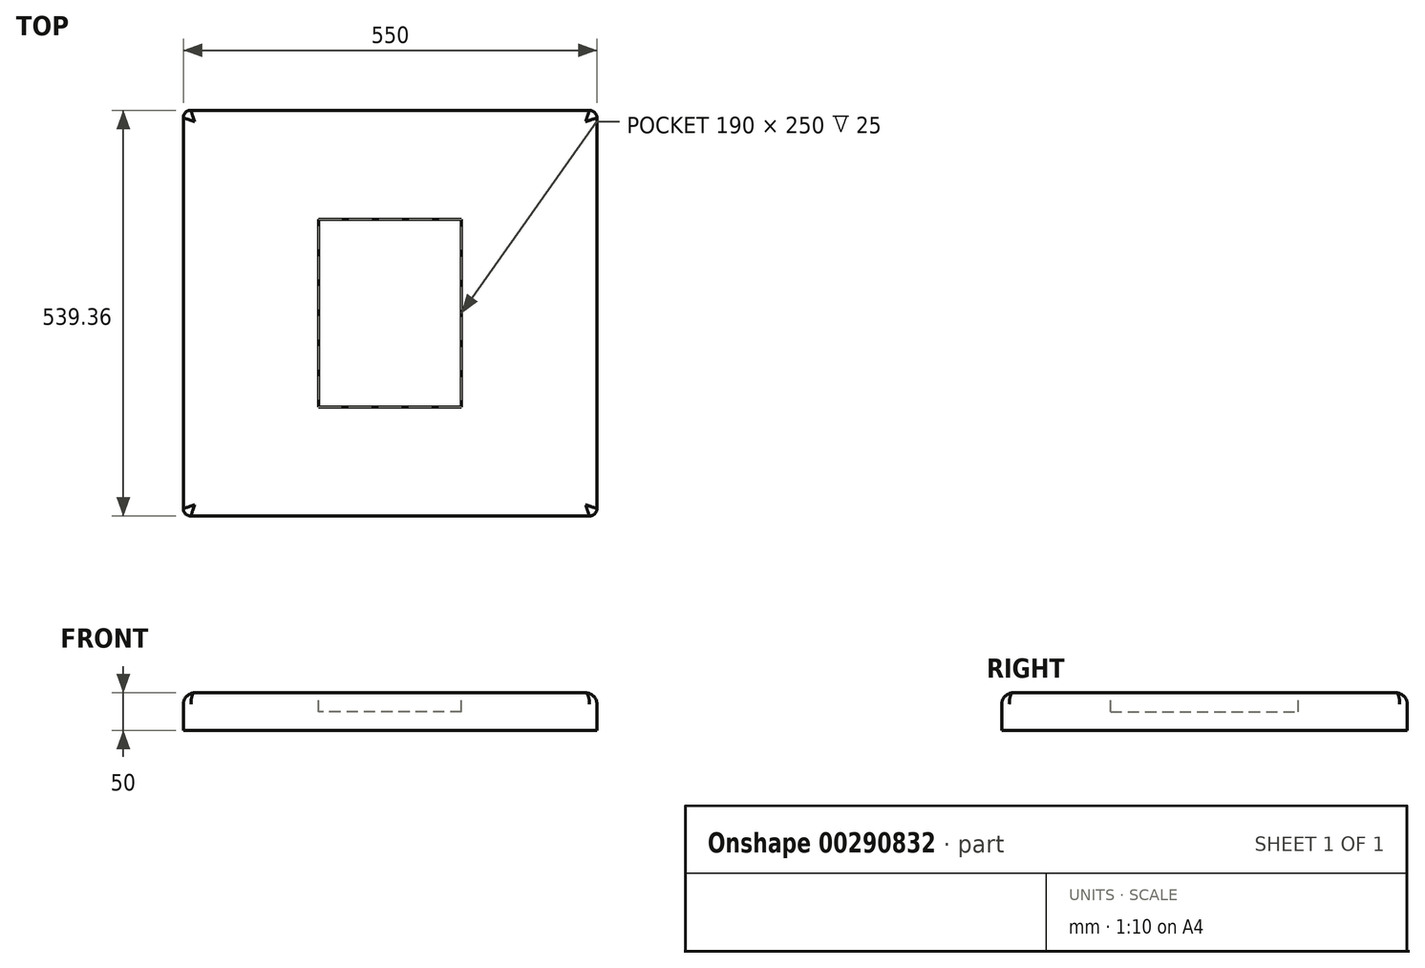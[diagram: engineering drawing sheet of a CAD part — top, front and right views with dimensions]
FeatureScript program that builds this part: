
annotation { "Feature Type Name" : "Feature", "Feature Type Description" : "" }
export const myFeature = defineFeature(function(context is Context, id is Id, definition is map)
    precondition{}
    {
        {
            var Q0;
            Q0=qCreatedBy(makeId("Top.planeOp"),FACE);
            var sketch = newSketch(context, id + "F0", { "sketchPlane" : qUnion([Q0])});
            skLineSegment(sketch, "E0.bottom", {"start": v(275, -269.68) * mm, "end": v(-275, -269.68) * mm});
            skLineSegment(sketch, "E0.top", {"start": v(275, 269.68) * mm, "end": v(-275, 269.68) * mm});
            skLineSegment(sketch, "E0.left", {"start": v(275, -269.68) * mm, "end": v(275, 269.68) * mm});
            skLineSegment(sketch, "E0.right", {"start": v(-275, -269.68) * mm, "end": v(-275, 269.68) * mm});
            skPoint(sketch, "E0.middle", {"position": v(0, 0) * mm});
            skSolve(sketch);
        }
        {
            var Q0;
            Q0=makeQuery(id+"F0.imprint","IMPRINT",FACE,{"disambiguationData":[TD([[makeQuery(id+"F0.imprint","IMPRINT",EDGE,{"derivedFrom":sQuery(id+"F0.wireOp",EDGE,"E0.bottom")}),-1.0]])]});
            extrude(context, id + "F1", {"entities" : qUnion([Q0]), "depth" : 50 * mm});
        }
        {
            var Q0;
            Q0=makeQuery(id+"F1.opExtrude","CAP_EDGE",EDGE,{"disambiguationData":[OSD([sQuery(id+"F0.wireOp",EDGE,"E0.bottom")])],"isStart":false});
            var Q1;
            Q1=makeQuery(id+"F1.opExtrude","CAP_EDGE",EDGE,{"disambiguationData":[OSD([sQuery(id+"F0.wireOp",EDGE,"E0.left")])],"isStart":false});
            var Q2;
            Q2=makeQuery(id+"F1.opExtrude","CAP_EDGE",EDGE,{"disambiguationData":[OSD([sQuery(id+"F0.wireOp",EDGE,"E0.top")])],"isStart":false});
            var Q3;
            Q3=makeQuery(id+"F1.opExtrude","CAP_EDGE",EDGE,{"disambiguationData":[OSD([sQuery(id+"F0.wireOp",EDGE,"E0.right")])],"isStart":false});
            fillet(context, id + "F2", {"entities" : qUnion([Q0, Q1, Q2, Q3]), "radius" : 15 * mm, "tangentPropagation" : true, "allowEdgeOverflow" : false});
        }
        {
            var Q0;
            Q0=makeQuery(id+"F1.opExtrude","CAP_FACE",FACE,{"disambiguationData":[OSD([sQuery(id+"F0.wireOp",EDGE,"E0.bottom"),sQuery(id+"F0.wireOp",EDGE,"E0.top"),sQuery(id+"F0.wireOp",EDGE,"E0.left"),sQuery(id+"F0.wireOp",EDGE,"E0.right")])],"isStart":false});
            var sketch = newSketch(context, id + "F3", { "sketchPlane" : qUnion([Q0])});
            skLineSegment(sketch, "E1.bottom", {"start": v(95, -125) * mm, "end": v(-95, -125) * mm});
            skLineSegment(sketch, "E1.top", {"start": v(95, 125) * mm, "end": v(-95, 125) * mm});
            skLineSegment(sketch, "E1.left", {"start": v(95, -125) * mm, "end": v(95, 125) * mm});
            skLineSegment(sketch, "E1.right", {"start": v(-95, -125) * mm, "end": v(-95, 125) * mm});
            skPoint(sketch, "E1.middle", {"position": v(0, 0) * mm});
            skSolve(sketch);
        }
        {
            var Q0;
            Q0=makeQuery(id+"F3.imprint","IMPRINT",FACE,{"disambiguationData":[TD([[makeQuery(id+"F3.imprint","IMPRINT",EDGE,{"derivedFrom":sQuery(id+"F3.wireOp",EDGE,"E1.bottom")}),-1.0]])]});
            extrude(context, id + "F4", {"entities" : qUnion([Q0]), "operationType" : NewBodyOperationType.REMOVE, "oppositeDirection" : true, "depth" : 25 * mm});
        }
        {
            var Q0;
            Q0=makeQuery(id+"F1.opExtrude","SWEPT_EDGE",EDGE,{"disambiguationData":[OSD([sQuery(id+"F0.wireOp",EDGE,"E0.bottom"),sQuery(id+"F0.wireOp",EDGE,"E0.left")])]});
            fillet(context, id + "F5", {"entities" : qUnion([Q0]), "radius" : 10 * mm, "tangentPropagation" : true, "allowEdgeOverflow" : false});
        }
        {
            var Q0;
            Q0=makeQuery(id+"F1.opExtrude","SWEPT_EDGE",EDGE,{"disambiguationData":[OSD([sQuery(id+"F0.wireOp",EDGE,"E0.bottom"),sQuery(id+"F0.wireOp",EDGE,"E0.right")])]});
            fillet(context, id + "F6", {"entities" : qUnion([Q0]), "radius" : 10 * mm, "tangentPropagation" : true, "allowEdgeOverflow" : false});
        }
        {
            var Q0;
            Q0=makeQuery(id+"F1.opExtrude","SWEPT_EDGE",EDGE,{"disambiguationData":[OSD([sQuery(id+"F0.wireOp",EDGE,"E0.top"),sQuery(id+"F0.wireOp",EDGE,"E0.left")])]});
            fillet(context, id + "F7", {"entities" : qUnion([Q0]), "radius" : 10 * mm, "tangentPropagation" : true, "allowEdgeOverflow" : false});
        }
        {
            var Q0;
            Q0=makeQuery(id+"F1.opExtrude","SWEPT_EDGE",EDGE,{"disambiguationData":[OSD([sQuery(id+"F0.wireOp",EDGE,"E0.top"),sQuery(id+"F0.wireOp",EDGE,"E0.right")])]});
            fillet(context, id + "F8", {"entities" : qUnion([Q0]), "radius" : 10 * mm, "tangentPropagation" : true, "allowEdgeOverflow" : false});
        }
    });
